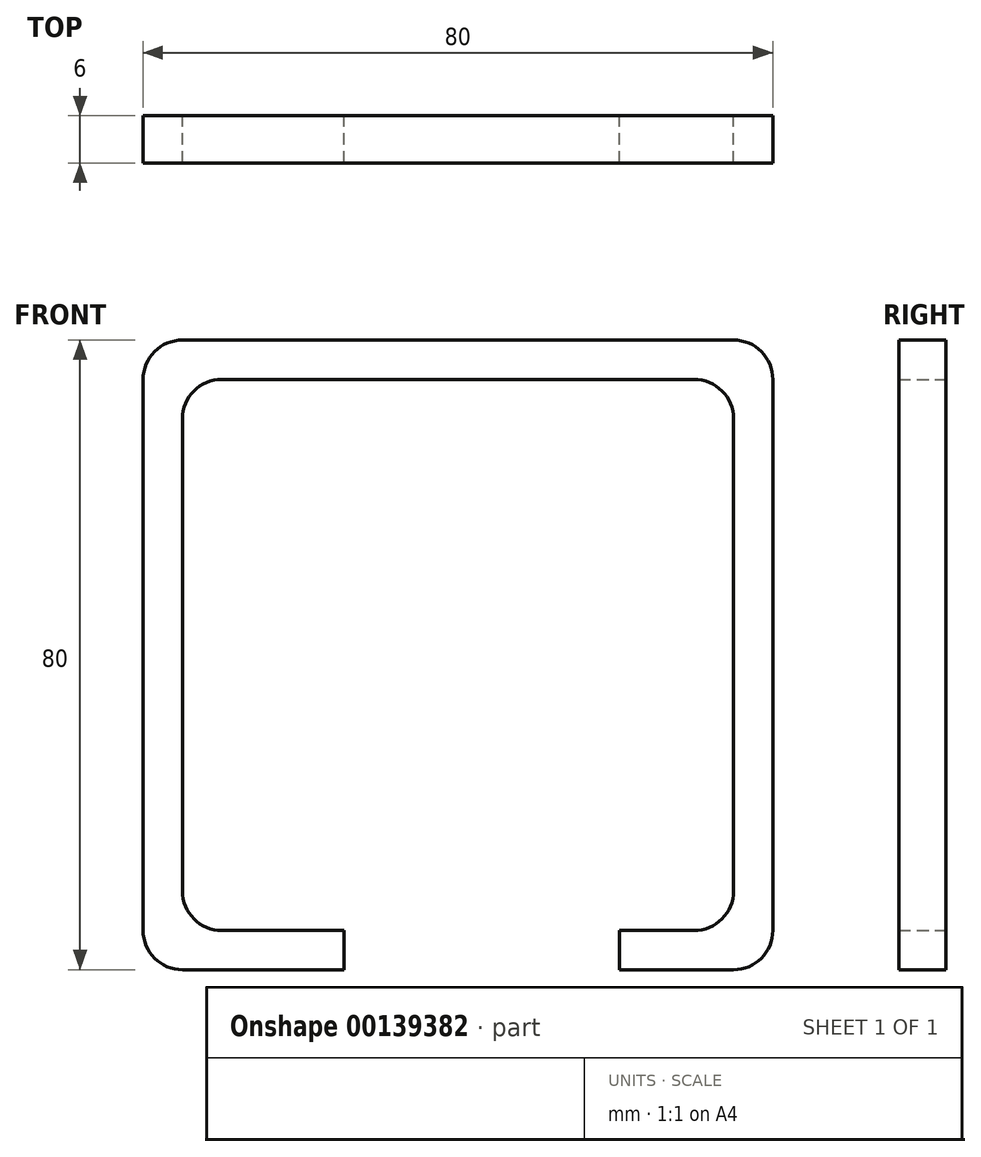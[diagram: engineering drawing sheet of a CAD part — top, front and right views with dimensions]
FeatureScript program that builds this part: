
annotation { "Feature Type Name" : "Feature", "Feature Type Description" : "" }
export const myFeature = defineFeature(function(context is Context, id is Id, definition is map)
    precondition{}
    {
        {
            var Q0;
            Q0=qCreatedBy(makeId("Front.planeOp"),FACE);
            var sketch = newSketch(context, id + "F0", { "sketchPlane" : qUnion([Q0])});
            skLineSegment(sketch, "E0.bottom", {"start": v(-5, 0) * mm, "end": v(-19.5, 0) * mm});
            skLineSegment(sketch, "E0.top", {"start": v(-5, 80) * mm, "end": v(-75, 80) * mm});
            skLineSegment(sketch, "E0.left", {"start": v(0, 5) * mm, "end": v(0, 75) * mm});
            skLineSegment(sketch, "E0.right", {"start": v(-80, 5) * mm, "end": v(-80, 75) * mm});
            skPoint(sketch, "E1.visualSharp", {"position": v(-80, 80) * mm});
            skArc(sketch, "E1.filletArc", {"start": v(-75, 80) * mm, "mid": v(-78.54, 78.54) * mm, "end": v(-80, 75) * mm});
            skPoint(sketch, "E2.visualSharp", {"position": v(0, 80) * mm});
            skArc(sketch, "E2.filletArc", {"start": v(0, 75) * mm, "mid": v(-1.46, 78.54) * mm, "end": v(-5, 80) * mm});
            skPoint(sketch, "E3.visualSharp", {"position": v(-80, 0) * mm});
            skArc(sketch, "E3.filletArc", {"start": v(-80, 5) * mm, "mid": v(-78.54, 1.46) * mm, "end": v(-75, 0) * mm});
            skPoint(sketch, "E4.visualSharp", {"position": v(0, 0) * mm});
            skArc(sketch, "E4.filletArc", {"start": v(-5, 0) * mm, "mid": v(-1.46, 1.46) * mm, "end": v(0, 5) * mm});
            skLineSegment(sketch, "E5.bottom", {"start": v(-70, 75) * mm, "end": v(-10, 75) * mm});
            skLineSegment(sketch, "E5.top", {"start": v(-70, 5) * mm, "end": v(-54.5, 5) * mm});
            skLineSegment(sketch, "E5.left", {"start": v(-75, 70) * mm, "end": v(-75, 10) * mm});
            skLineSegment(sketch, "E5.right", {"start": v(-5, 70) * mm, "end": v(-5, 10) * mm});
            skArc(sketch, "E6.filletArc", {"start": v(-70, 75) * mm, "mid": v(-73.54, 73.54) * mm, "end": v(-75, 70) * mm});
            skArc(sketch, "E7.filletArc", {"start": v(-5, 70) * mm, "mid": v(-6.46, 73.54) * mm, "end": v(-10, 75) * mm});
            skArc(sketch, "E8.filletArc", {"start": v(-10, 5) * mm, "mid": v(-6.46, 6.46) * mm, "end": v(-5, 10) * mm});
            skArc(sketch, "E9.filletArc", {"start": v(-75, 10) * mm, "mid": v(-73.54, 6.46) * mm, "end": v(-70, 5) * mm});
            skLineSegment(sketch, "E10", {"start": v(-54.5, 0) * mm, "end": v(-54.5, 5) * mm});
            skLineSegment(sketch, "E11", {"start": v(-19.5, 5) * mm, "end": v(-19.5, 0) * mm});
            skLineSegment(sketch, "E12.trimOffspring", {"start": v(-19.5, 5) * mm, "end": v(-10, 5) * mm});
            skLineSegment(sketch, "E13.trimOffspring", {"start": v(-54.5, 0) * mm, "end": v(-75, 0) * mm});
            skSolve(sketch);
        }
        {
            var Q0;
            Q0=makeQuery(id+"F0.imprint","IMPRINT",FACE,{"disambiguationData":[TD([[makeQuery(id+"F0.imprint","IMPRINT",EDGE,{"derivedFrom":sQuery(id+"F0.wireOp",EDGE,"E0.bottom")}),-1.0]])]});
            extrude(context, id + "F1", {"entities" : qUnion([Q0]), "depth" : 6 * mm});
        }
    });
